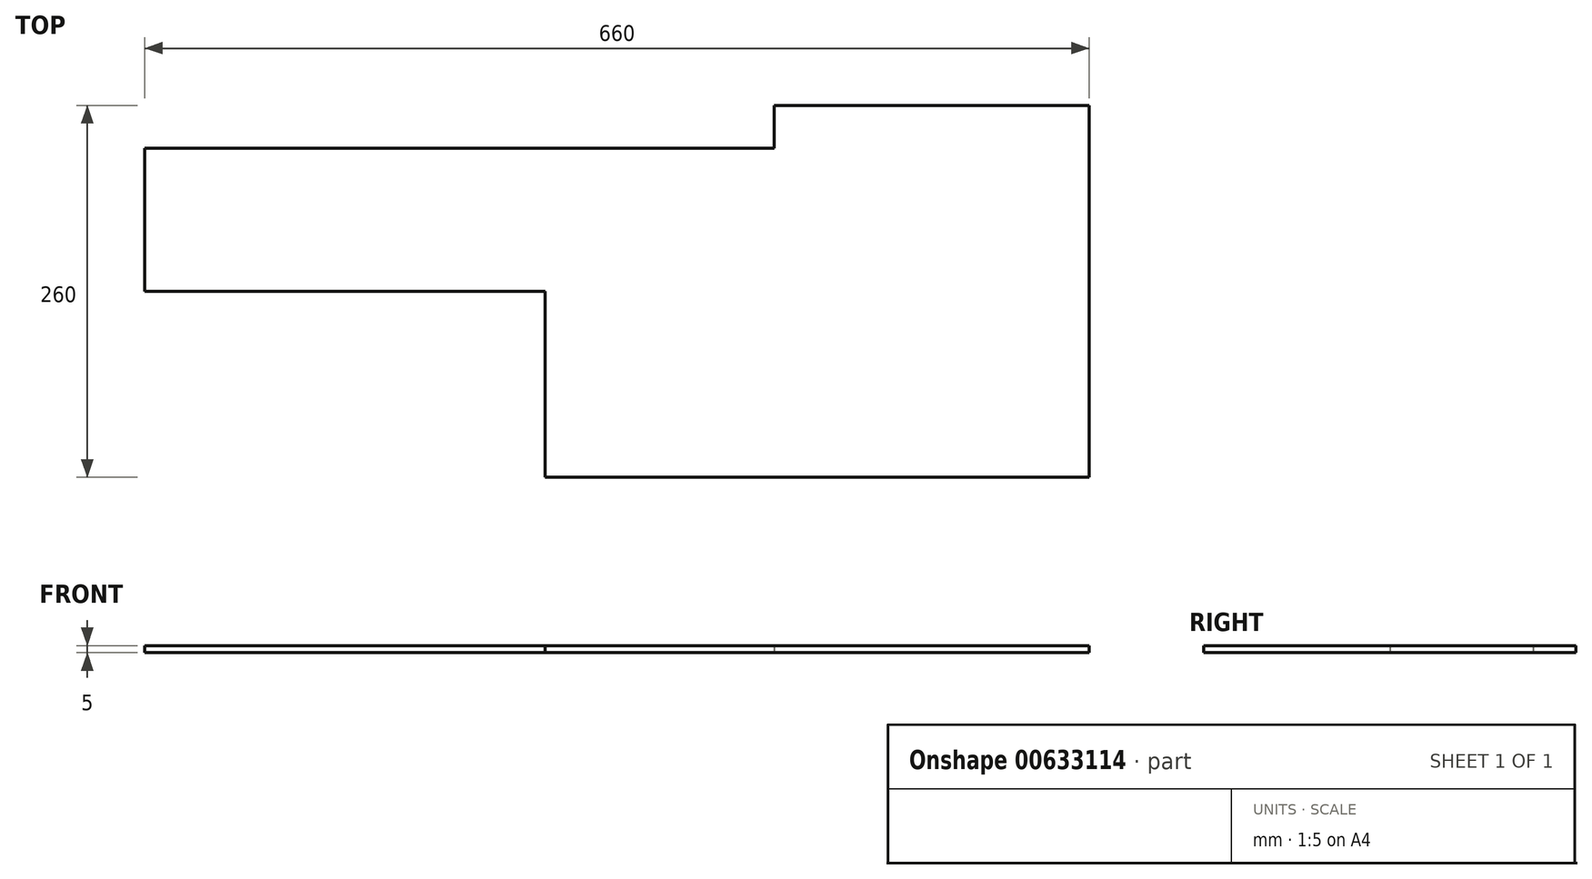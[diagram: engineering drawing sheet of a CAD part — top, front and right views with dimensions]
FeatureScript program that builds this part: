
annotation { "Feature Type Name" : "Feature", "Feature Type Description" : "" }
export const myFeature = defineFeature(function(context is Context, id is Id, definition is map)
    precondition{}
    {
        {
            var Q0;
            Q0=qCreatedBy(makeId("Top.planeOp"),FACE);
            var sketch = newSketch(context, id + "F0", { "sketchPlane" : qUnion([Q0])});
            skLineSegment(sketch, "E0.bottom", {"start": v(0, 0) * mm, "end": v(380, 0) * mm});
            skLineSegment(sketch, "E0.top", {"start": v(160, 260) * mm, "end": v(380, 260) * mm});
            skLineSegment(sketch, "E0.left", {"start": v(-280, 130) * mm, "end": v(-280, 230) * mm});
            skLineSegment(sketch, "E0.right", {"start": v(380, 0) * mm, "end": v(380, 260) * mm});
            skLineSegment(sketch, "E1", {"start": v(-280, 130) * mm, "end": v(0, 130) * mm});
            skLineSegment(sketch, "E2", {"start": v(0, 130) * mm, "end": v(0, 0) * mm});
            skLineSegment(sketch, "E3", {"start": v(-280, 230) * mm, "end": v(160, 230) * mm});
            skLineSegment(sketch, "E4", {"start": v(160, 230) * mm, "end": v(160, 260) * mm});
            skSolve(sketch);
        }
        {
            var Q0;
            Q0=makeQuery(id+"F0.imprint","IMPRINT",FACE,{"disambiguationData":[TD([[makeQuery(id+"F0.imprint","IMPRINT",EDGE,{"derivedFrom":sQuery(id+"F0.wireOp",EDGE,"E0.bottom")}),1.0]])]});
            extrude(context, id + "F1", {"entities" : qUnion([Q0]), "depth" : 5 * mm, "offsetDistance" : 25 * mm});
        }
    });
